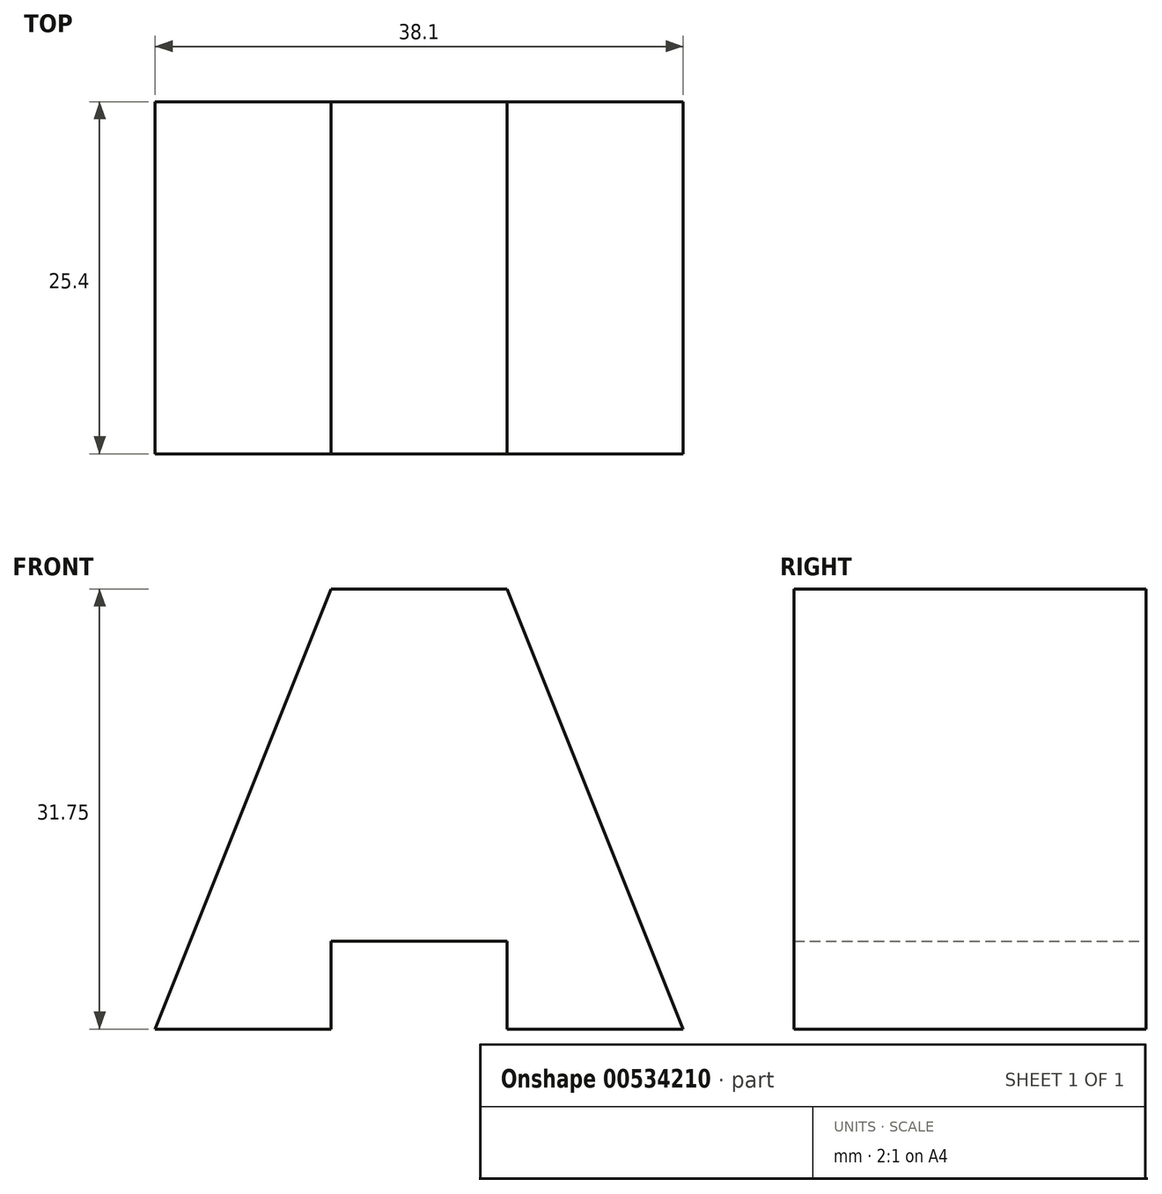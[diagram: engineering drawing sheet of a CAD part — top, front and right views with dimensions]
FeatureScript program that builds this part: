
annotation { "Feature Type Name" : "Feature", "Feature Type Description" : "" }
export const myFeature = defineFeature(function(context is Context, id is Id, definition is map)
    precondition{}
    {
        {
            var Q0;
            Q0=qCreatedBy(makeId("Front.planeOp"),FACE);
            var sketch = newSketch(context, id + "F0", { "sketchPlane" : qUnion([Q0])});
            skLineSegment(sketch, "E0", {"start": v(0, 0) * mm, "end": v(38.1, 0) * mm});
            skLineSegment(sketch, "E1", {"start": v(38.1, 0) * mm, "end": v(25.4, 31.75) * mm});
            skLineSegment(sketch, "E2", {"start": v(25.4, 31.75) * mm, "end": v(12.7, 31.75) * mm});
            skLineSegment(sketch, "E3", {"start": v(12.7, 31.75) * mm, "end": v(0, 0) * mm});
            skLineSegment(sketch, "E4", {"start": v(0, 0) * mm, "end": v(12.7, 0) * mm});
            skLineSegment(sketch, "E5", {"start": v(12.7, 0) * mm, "end": v(12.7, 6.35) * mm});
            skLineSegment(sketch, "E6", {"start": v(12.7, 6.35) * mm, "end": v(25.4, 6.35) * mm});
            skLineSegment(sketch, "E7", {"start": v(25.4, 6.35) * mm, "end": v(25.4, 0) * mm});
            skLineSegment(sketch, "E8", {"start": v(25.4, 0) * mm, "end": v(38.1, 0) * mm});
            skSolve(sketch);
        }
        {
            var Q0;
            Q0=makeQuery(id+"F0.imprint","IMPRINT",FACE,{"disambiguationData":[TD([[makeQuery(id+"F0.imprint","IMPRINT",EDGE,{"derivedFrom":sQuery(id+"F0.wireOp",EDGE,"E1")}),1.0]])]});
            extrude(context, id + "F1", {"entities" : qUnion([Q0]), "depth" : 25.4 * mm, "offsetDistance" : 25.4 * mm});
        }
    });
